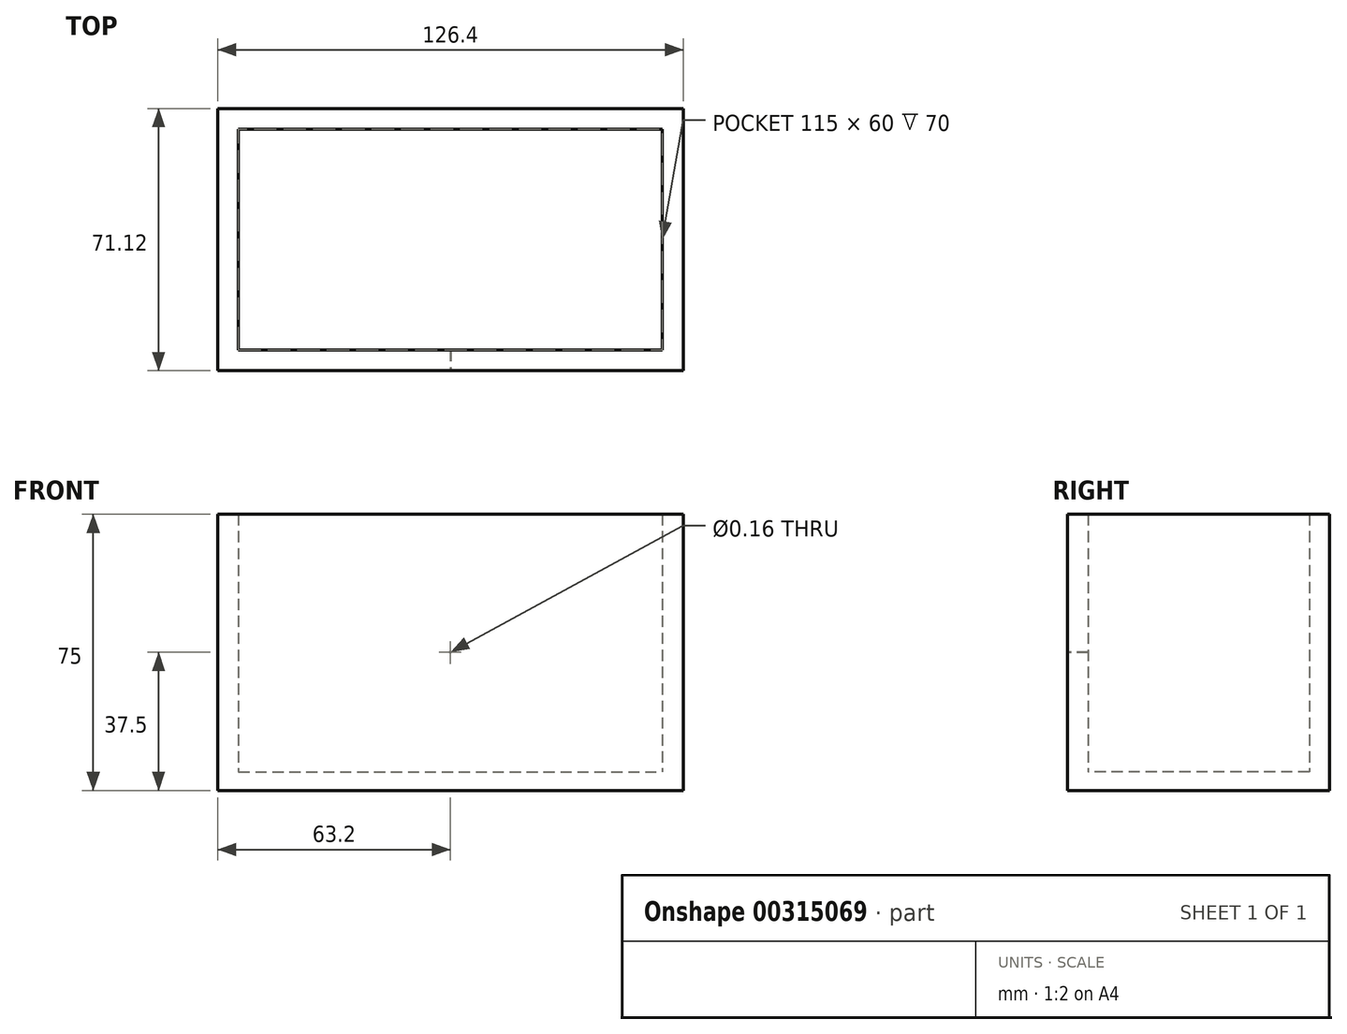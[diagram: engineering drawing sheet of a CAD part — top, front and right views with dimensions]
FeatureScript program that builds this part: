
annotation { "Feature Type Name" : "Feature", "Feature Type Description" : "" }
export const myFeature = defineFeature(function(context is Context, id is Id, definition is map)
    precondition{}
    {
        {
            var Q0;
            Q0=qCreatedBy(makeId("Top.planeOp"),FACE);
            var sketch = newSketch(context, id + "F0", { "sketchPlane" : qUnion([Q0])});
            skLineSegment(sketch, "E0.bottom", {"start": v(-57.5, 30) * mm, "end": v(57.5, 30) * mm});
            skLineSegment(sketch, "E0.top", {"start": v(-57.5, -30) * mm, "end": v(57.5, -30) * mm});
            skLineSegment(sketch, "E0.left", {"start": v(-57.5, 30) * mm, "end": v(-57.5, -30) * mm});
            skLineSegment(sketch, "E0.right", {"start": v(57.5, 30) * mm, "end": v(57.5, -30) * mm});
            skPoint(sketch, "E0.middle", {"position": v(0, 0) * mm});
            skSolve(sketch);
        }
        {
            var Q0;
            Q0=makeQuery(id+"F0.imprint","IMPRINT",FACE,{"disambiguationData":[TD([[makeQuery(id+"F0.imprint","IMPRINT",EDGE,{"derivedFrom":sQuery(id+"F0.wireOp",EDGE,"E0.bottom")}),-1.0]])]});
            var sketch = newSketch(context, id + "F1", { "sketchPlane" : qUnion([Q0])});
            skLineSegment(sketch, "E1.bottom", {"start": v(-63.2, 35.56) * mm, "end": v(63.2, 35.56) * mm});
            skLineSegment(sketch, "E1.top", {"start": v(-63.2, -35.56) * mm, "end": v(63.2, -35.56) * mm});
            skLineSegment(sketch, "E1.left", {"start": v(-63.2, 35.56) * mm, "end": v(-63.2, -35.56) * mm});
            skLineSegment(sketch, "E1.right", {"start": v(63.2, 35.56) * mm, "end": v(63.2, -35.56) * mm});
            skPoint(sketch, "E1.middle", {"position": v(0, 0) * mm});
            skSolve(sketch);
        }
        {
            var Q0;
            Q0=makeQuery(id+"F0.imprint","IMPRINT",FACE,{"disambiguationData":[TD([[makeQuery(id+"F0.imprint","IMPRINT",EDGE,{"derivedFrom":sQuery(id+"F0.wireOp",EDGE,"E0.bottom")}),-1.0]])]});
            extrude(context, id + "F2", {"entities" : qUnion([Q0]), "depth" : 5 * mm});
        }
        {
            var Q0;
            Q0=makeQuery(id+"F1.imprint","IMPRINT",FACE,{"disambiguationData":[TD([[makeQuery(id+"F1.imprint","IMPRINT",EDGE,{"derivedFrom":sQuery(id+"F1.wireOp",EDGE,"E1.bottom")}),-1.0]])]});
            extrude(context, id + "F3", {"entities" : qUnion([Q0]), "operationType" : NewBodyOperationType.ADD, "depth" : 75 * mm});
        }
        {
            var Q0;
            Q0=makeQuery(id+"F3.opExtrude","SWEPT_FACE",FACE,{"disambiguationData":[OSD([sQuery(id+"F1.wireOp",EDGE,"E1.top")])]});
            var sketch = newSketch(context, id + "F4", { "sketchPlane" : qUnion([Q0])});
            skLineSegment(sketch, "E2", {"start": v(0, 75) * mm, "end": v(0, 0) * mm, "construction": true});
            skPoint(sketch, "E3", {"position": v(0, 37.5) * mm});
            skCircle(sketch, "E4", {"center": v(0, 37.5) * mm, "radius": 0.08 * mm});
            skSolve(sketch);
        }
        {
            var Q0;
            Q0=makeQuery(id+"F4.imprint","IMPRINT",FACE,{"disambiguationData":[TD([[makeQuery(id+"F4.imprint","IMPRINT",EDGE,{"derivedFrom":sQuery(id+"F4.wireOp",EDGE,"E4")}),1.0]])]});
            extrude(context, id + "F5", {"entities" : qUnion([Q0]), "operationType" : NewBodyOperationType.REMOVE, "oppositeDirection" : true, "depth" : 7.54 * mm});
        }
    });
